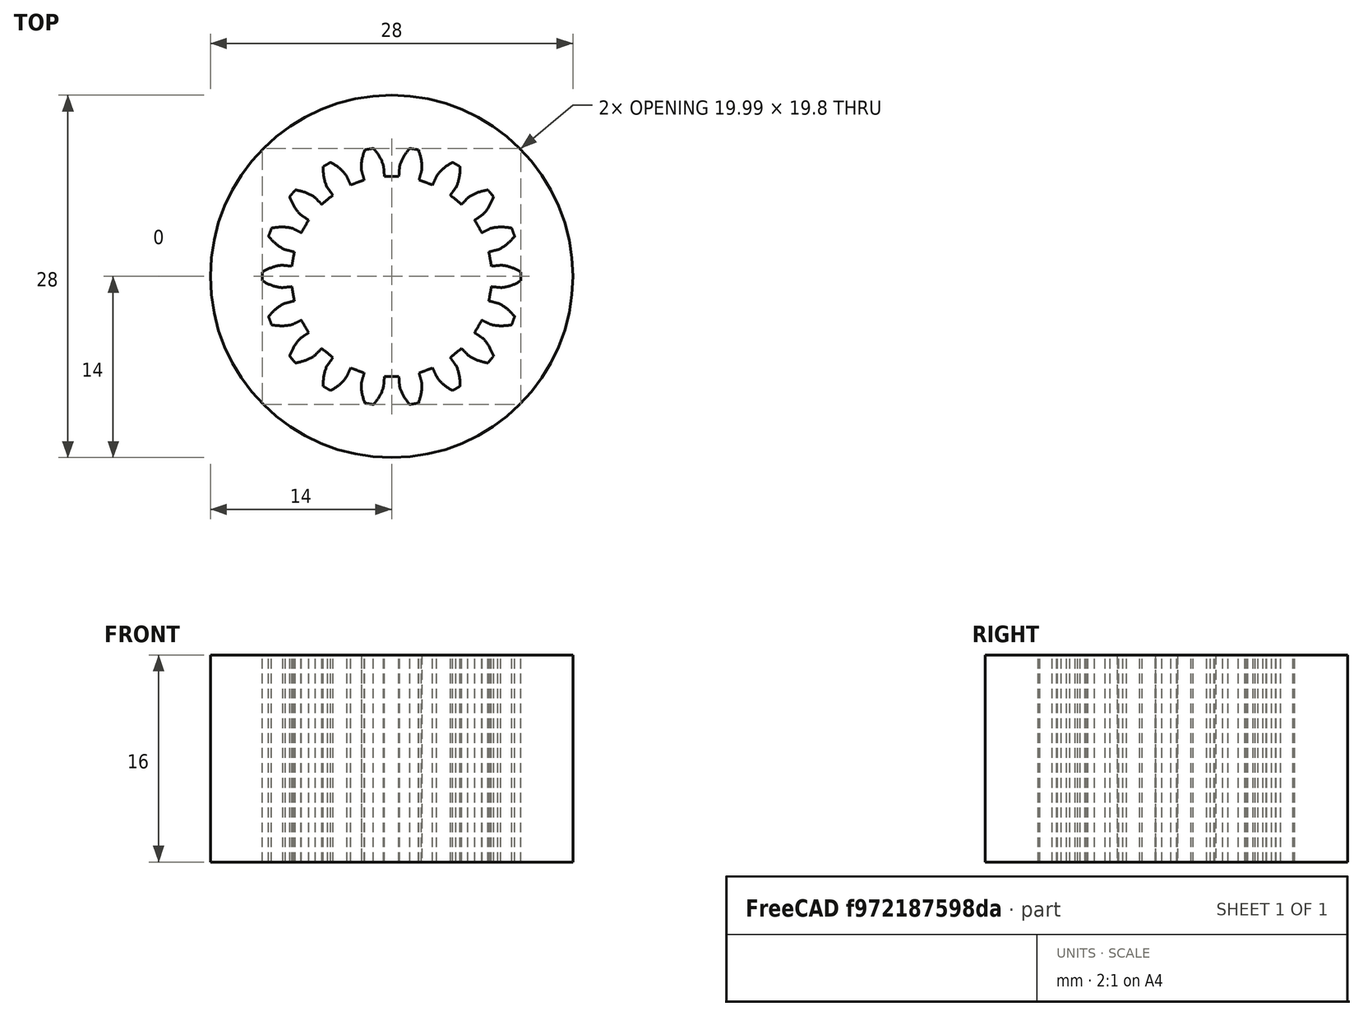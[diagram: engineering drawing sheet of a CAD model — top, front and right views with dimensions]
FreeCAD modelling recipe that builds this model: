
FCSTD DOCUMENT  (FreeCAD 0.19R24276 (Git))
Label: Gear_privod_perehodnik_to_GT2_part_d28
License: All rights reserved
LicenseURL: http://en.wikipedia.org/wiki/All_rights_reserved
objects: Sketcher::SketchObject×1, PartDesign::FeaturePython×1, PartDesign::Pad×1, PartDesign::Body×1, Part::Cut×1
note: 6 computed .brp shape members not serialized (recipe doc carries the construction recipe); baked Part::Feature solids carry a one-line shape summary decoded from their .brp

FEATURE [Sketcher::SketchObject] Sketch  label="Sketch_d28"
  FullyConstrained = true
  MapMode = 5
  Support = -> [XY_Plane]
  sketch-geometry (1):
    g0: Circle CenterX=0 CenterY=0 CenterZ=0 NormalX=0 NormalY=0 NormalZ=1 AngleXU=0 Radius=14
  constraints (2):
    c: Coincident(g0,g-1)
    c: Diameter(g0) = 28
FEATURE [PartDesign::FeaturePython] involutegear  # WARN: FeaturePython — macro-defined, semantics opaque (R4)
  AttacherType = Attacher::AttachEngine3D
  backlash = 0
  beta = 0
  clearance = 0.25
  da = 20
  df = 15.5
  double_helix = false
  dw = 18
  head = 0
  height = 16
  module = 1
  numpoints = 6
  pressure_angle = 20
  properties_from_tool = false
  reversed_backlash = false
  shift = 0
  simple = false
  teeth = 18
  transverse_pitch = 3.14159
  undercut = false
  version = 0.0.3
FEATURE [PartDesign::Pad] Pad  label="Pad_h16"
  BaseFeature = -> involutegear
  Direction = (1,1,1)
  Length = 16
  Length2 = 100
  Profile = -> Sketch
  Type = 0
FEATURE [PartDesign::Body] Body
  Group = -> [Sketch,involutegear,Pad]
  Origin = -> Origin
  Tip = -> Pad
FEATURE [Part::Cut] Cut
  Base = -> Pad
  Tool = -> involutegear
